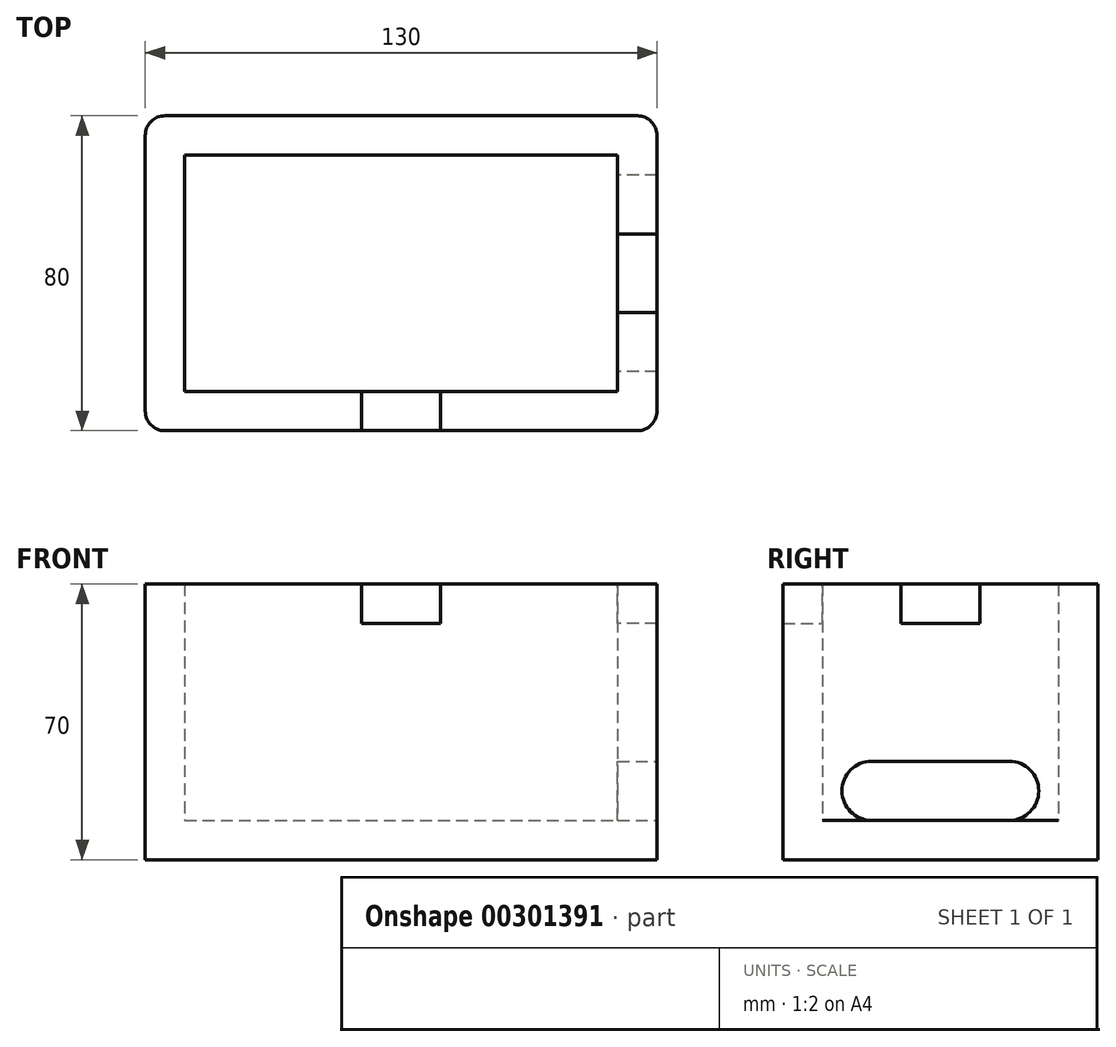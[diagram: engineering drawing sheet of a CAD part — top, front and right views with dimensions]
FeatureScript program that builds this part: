
annotation { "Feature Type Name" : "Feature", "Feature Type Description" : "" }
export const myFeature = defineFeature(function(context is Context, id is Id, definition is map)
    precondition{}
    {
        {
            var Q0;
            Q0=qCreatedBy(makeId("Top.planeOp"),FACE);
            var sketch = newSketch(context, id + "F0", { "sketchPlane" : qUnion([Q0])});
            skLineSegment(sketch, "E0", {"start": v(-0.63, 30) * mm, "end": v(-55, 30) * mm});
            skLineSegment(sketch, "E1.MirrorCS", {"start": v(0.63, 30) * mm, "end": v(55, 30) * mm});
            skLineSegment(sketch, "E2.MirrorCS", {"start": v(-0.63, -30) * mm, "end": v(-55, -30) * mm});
            skLineSegment(sketch, "E3.MirrorCS", {"start": v(0.63, -30) * mm, "end": v(55, -30) * mm});
            skLineSegment(sketch, "E4", {"start": v(-55, 30) * mm, "end": v(-55, -30) * mm});
            skLineSegment(sketch, "E5", {"start": v(55, -30) * mm, "end": v(55, 30) * mm});
            skLineSegment(sketch, "E6", {"start": v(-55, 40) * mm, "end": v(55, 40) * mm});
            skLineSegment(sketch, "E7", {"start": v(55, 40) * mm, "end": v(65, 40) * mm});
            skLineSegment(sketch, "E8", {"start": v(65, 40) * mm, "end": v(65, -30) * mm});
            skLineSegment(sketch, "E9", {"start": v(65, -30) * mm, "end": v(65, -40) * mm});
            skLineSegment(sketch, "E10", {"start": v(65, -40) * mm, "end": v(-55, -40) * mm});
            skLineSegment(sketch, "E11", {"start": v(-55, -40) * mm, "end": v(-65, -40) * mm});
            skLineSegment(sketch, "E12", {"start": v(-55, 40) * mm, "end": v(-65, 40) * mm});
            skLineSegment(sketch, "E13", {"start": v(-65, 40) * mm, "end": v(-65, -40) * mm});
            skSolve(sketch);
        }
        {
            var Q0;
            Q0 = qSketchRegion(id + "F0", true);
            extrude(context, id + "F1", {"entities" : qUnion([Q0]), "depth" : 10 * mm});
        }
        {
            var Q0;
            Q0=makeQuery(id+"F1.opExtrude","CAP_FACE",FACE,{"disambiguationData":[OSD([sQuery(id+"F0.wireOp",EDGE,"E6"),sQuery(id+"F0.wireOp",EDGE,"E7"),sQuery(id+"F0.wireOp",EDGE,"E8"),sQuery(id+"F0.wireOp",EDGE,"E9"),sQuery(id+"F0.wireOp",EDGE,"E10"),sQuery(id+"F0.wireOp",EDGE,"E11"),sQuery(id+"F0.wireOp",EDGE,"E12"),sQuery(id+"F0.wireOp",EDGE,"E13")])],"isStart":false});
            var sketch = newSketch(context, id + "F2", { "sketchPlane" : qUnion([Q0])});
            skLineSegment(sketch, "E14", {"start": v(-55, 30) * mm, "end": v(-55, -30) * mm});
            skLineSegment(sketch, "E15", {"start": v(-55, 30) * mm, "end": v(55, 30) * mm});
            skLineSegment(sketch, "E16.MirrorCS", {"start": v(55, 30) * mm, "end": v(55, -30) * mm});
            skLineSegment(sketch, "E17.MirrorCS", {"start": v(-55, -30) * mm, "end": v(55, -30) * mm});
            skLineSegment(sketch, "E18.0.0", {"start": v(65, 40) * mm, "end": v(-65, 40) * mm});
            skLineSegment(sketch, "E18.0.1", {"start": v(-65, 40) * mm, "end": v(-65, -40) * mm});
            skLineSegment(sketch, "E18.0.2", {"start": v(-65, -40) * mm, "end": v(65, -40) * mm});
            skLineSegment(sketch, "E18.0.3", {"start": v(65, -40) * mm, "end": v(65, 40) * mm});
            skPoint(sketch, "E19.orphan", {"position": v(-55, 40) * mm});
            skPoint(sketch, "E20.orphan", {"position": v(-65, 30) * mm});
            skPoint(sketch, "E21.orphan", {"position": v(65, 30) * mm});
            skPoint(sketch, "E22.orphan", {"position": v(55, 40) * mm});
            skPoint(sketch, "E23.orphan", {"position": v(65, -30) * mm});
            skPoint(sketch, "E24.orphan", {"position": v(55, -40) * mm});
            skPoint(sketch, "E25.orphan", {"position": v(-55, -40) * mm});
            skPoint(sketch, "E26.orphan", {"position": v(-65, -30) * mm});
            skSolve(sketch);
        }
        {
            var Q0;
            Q0=makeQuery(id+"F2.imprint","IMPRINT",FACE,{"disambiguationData":[TD([[makeQuery(id+"F2.imprint","IMPRINT",EDGE,{"derivedFrom":sQuery(id+"F2.wireOp",EDGE,"E14")}),-1.0]])]});
            extrude(context, id + "F3", {"entities" : qUnion([Q0]), "operationType" : NewBodyOperationType.ADD, "depth" : 60 * mm});
        }
        {
            var Q0;
            Q0=makeQuery(id+"F3.opExtrude","CAP_FACE",FACE,{"disambiguationData":[OSD([sQuery(id+"F2.wireOp",EDGE,"E14"),sQuery(id+"F2.wireOp",EDGE,"E15"),sQuery(id+"F2.wireOp",EDGE,"E16.MirrorCS"),sQuery(id+"F2.wireOp",EDGE,"E17.MirrorCS"),sQuery(id+"F2.wireOp",EDGE,"E18.0.0"),sQuery(id+"F2.wireOp",EDGE,"E18.0.1"),sQuery(id+"F2.wireOp",EDGE,"E18.0.2"),sQuery(id+"F2.wireOp",EDGE,"E18.0.3")])],"isStart":false});
            var sketch = newSketch(context, id + "F4", { "sketchPlane" : qUnion([Q0])});
            skLineSegment(sketch, "E27.0.0", {"start": v(65, -40) * mm, "end": v(65, 40) * mm});
            skLineSegment(sketch, "E27.0.1", {"start": v(65, 40) * mm, "end": v(-65, 40) * mm});
            skLineSegment(sketch, "E27.0.2", {"start": v(-65, 40) * mm, "end": v(-65, -40) * mm});
            skLineSegment(sketch, "E27.0.3", {"start": v(-65, -40) * mm, "end": v(65, -40) * mm});
            skLineSegment(sketch, "E28", {"start": v(0, 40) * mm, "end": v(-10, 40) * mm});
            skLineSegment(sketch, "E29", {"start": v(-10, 40) * mm, "end": v(-10, 30) * mm});
            skLineSegment(sketch, "E30", {"start": v(-10, 30) * mm, "end": v(10, 30) * mm});
            skLineSegment(sketch, "E31", {"start": v(10, 30) * mm, "end": v(10, 40) * mm});
            skLineSegment(sketch, "E32", {"start": v(10, 40) * mm, "end": v(0, 40) * mm});
            skLineSegment(sketch, "E33.MirrorCS", {"start": v(-10, -40) * mm, "end": v(-10, -30) * mm});
            skLineSegment(sketch, "E34.MirrorCS", {"start": v(10, -30) * mm, "end": v(10, -40) * mm});
            skLineSegment(sketch, "E35", {"start": v(-65, 0) * mm, "end": v(-65, 10) * mm});
            skLineSegment(sketch, "E36", {"start": v(-65, 10) * mm, "end": v(-55, 10) * mm});
            skLineSegment(sketch, "E37.MirrorCS", {"start": v(-65, -10) * mm, "end": v(-55, -10) * mm});
            skLineSegment(sketch, "E38.MirrorCS", {"start": v(65, 10) * mm, "end": v(55, 10) * mm});
            skLineSegment(sketch, "E39.MirrorCS", {"start": v(65, -10) * mm, "end": v(55, -10) * mm});
            skSolve(sketch);
        }
        {
            var Q0;
            Q0=makeQuery(id+"F4.imprint","IMPRINT",FACE,{"disambiguationData":[TD([[makeQuery(id+"F4.imprint","IMPRINT",EDGE,{"derivedFrom":sQuery(id+"F4.wireOp",EDGE,"E28")}),1.0]])]});
            var Q1;
            {var subQ2=sQuery(id+"F4.wireOp",EDGE,"E35");Q1=makeQuery(id+"F4.imprint","IMPRINT",FACE,{"disambiguationData":[TD([[makeQuery(id+"F4.imprint","IMPRINT",EDGE,{"derivedFrom":subQ2}),1.0]])]});}
            var Q2;
            {var subQ0=sQuery(id+"F4.wireOp",EDGE,"E33.MirrorCS");Q2=makeQuery(id+"F4.imprint","IMPRINT",FACE,{"disambiguationData":[TD([[makeQuery(id+"F4.imprint","IMPRINT",EDGE,{"derivedFrom":subQ0}),-1.0]])]});}
            var Q3;
            {var subQ0=sQuery(id+"F4.wireOp",EDGE,"E38.MirrorCS");Q3=makeQuery(id+"F4.imprint","IMPRINT",FACE,{"disambiguationData":[TD([[makeQuery(id+"F4.imprint","IMPRINT",EDGE,{"derivedFrom":subQ0}),1.0]])]});}
            extrude(context, id + "F5", {"entities" : qUnion([Q0, Q1, Q2, Q3]), "operationType" : NewBodyOperationType.REMOVE, "oppositeDirection" : true, "depth" : 10 * mm});
        }
        {
            var Q0;
            Q0=makeQuery(id+"F3.boolean.opBoolean","MERGE",EDGE,{"derivedFrom":[makeQuery(id+"F1.opExtrude","SWEPT_EDGE",EDGE,{"disambiguationData":[OSD([sQuery(id+"F0.wireOp",EDGE,"E11"),sQuery(id+"F0.wireOp",EDGE,"E13")])]}),makeQuery(id+"F3.opExtrude","SWEPT_EDGE",EDGE,{"disambiguationData":[OSD([sQuery(id+"F2.wireOp",EDGE,"E18.0.1"),sQuery(id+"F2.wireOp",EDGE,"E18.0.2")])]})]});
            var Q1;
            Q1=makeQuery(id+"F3.boolean.opBoolean","MERGE",EDGE,{"derivedFrom":[makeQuery(id+"F1.opExtrude","SWEPT_EDGE",EDGE,{"disambiguationData":[OSD([sQuery(id+"F0.wireOp",EDGE,"E9"),sQuery(id+"F0.wireOp",EDGE,"E10")])]}),makeQuery(id+"F3.opExtrude","SWEPT_EDGE",EDGE,{"disambiguationData":[OSD([sQuery(id+"F2.wireOp",EDGE,"E18.0.2"),sQuery(id+"F2.wireOp",EDGE,"E18.0.3")])]})]});
            var Q2;
            Q2=makeQuery(id+"F3.boolean.opBoolean","MERGE",EDGE,{"derivedFrom":[makeQuery(id+"F1.opExtrude","SWEPT_EDGE",EDGE,{"disambiguationData":[OSD([sQuery(id+"F0.wireOp",EDGE,"E12"),sQuery(id+"F0.wireOp",EDGE,"E13")])]}),makeQuery(id+"F3.opExtrude","SWEPT_EDGE",EDGE,{"disambiguationData":[OSD([sQuery(id+"F2.wireOp",EDGE,"E18.0.0"),sQuery(id+"F2.wireOp",EDGE,"E18.0.1")])]})]});
            var Q3;
            Q3=makeQuery(id+"F3.boolean.opBoolean","MERGE",EDGE,{"derivedFrom":[makeQuery(id+"F1.opExtrude","SWEPT_EDGE",EDGE,{"disambiguationData":[OSD([sQuery(id+"F0.wireOp",EDGE,"E7"),sQuery(id+"F0.wireOp",EDGE,"E8")])]}),makeQuery(id+"F3.opExtrude","SWEPT_EDGE",EDGE,{"disambiguationData":[OSD([sQuery(id+"F2.wireOp",EDGE,"E18.0.0"),sQuery(id+"F2.wireOp",EDGE,"E18.0.3")])]})]});
            fillet(context, id + "F6", {"entities" : qUnion([Q0, Q1, Q2, Q3]), "radius" : 5 * mm, "tangentPropagation" : true, "allowEdgeOverflow" : false});
        }
        {
            var Q0;
            Q0=makeQuery(id+"F3.boolean.opBoolean","MERGE",FACE,{"derivedFrom":[makeQuery(id+"F1.opExtrude","SWEPT_FACE",FACE,{"disambiguationData":[OSD([sQuery(id+"F0.wireOp",EDGE,"E8"),sQuery(id+"F0.wireOp",EDGE,"E9")])]}),makeQuery(id+"F3.opExtrude","SWEPT_FACE",FACE,{"disambiguationData":[OSD([sQuery(id+"F2.wireOp",EDGE,"E18.0.3")])]})]});
            var sketch = newSketch(context, id + "F7", { "sketchPlane" : qUnion([Q0])});
            skLineSegment(sketch, "E40", {"start": v(0, 0) * mm, "end": v(0, 10) * mm});
            skLineSegment(sketch, "E41", {"start": v(0, 10) * mm, "end": v(-25, 10) * mm});
            skLineSegment(sketch, "E42", {"start": v(-25, 10) * mm, "end": v(-25, 25) * mm});
            skLineSegment(sketch, "E43", {"start": v(-25, 25) * mm, "end": v(25, 25) * mm});
            skLineSegment(sketch, "E44", {"start": v(25, 25) * mm, "end": v(25, 10) * mm});
            skLineSegment(sketch, "E45", {"start": v(25, 10) * mm, "end": v(0, 10) * mm});
            skSolve(sketch);
        }
        {
            var Q0;
            Q0 = qSketchRegion(id + "F7", true);
            extrude(context, id + "F8", {"entities" : qUnion([Q0]), "operationType" : NewBodyOperationType.REMOVE, "oppositeDirection" : true, "depth" : 25 * mm});
        }
        {
            var Q0;
            Q0=makeQuery(id+"F8.boolean.opBoolean","COPY",EDGE,{"derivedFrom":makeQuery(id+"F8.opExtrude","SWEPT_EDGE",EDGE,{"disambiguationData":[OSD([sQuery(id+"F7.wireOp",EDGE,"E43"),sQuery(id+"F7.wireOp",EDGE,"E44")])]})});
            var Q1;
            Q1=makeQuery(id+"F8.boolean.opBoolean","COPY",EDGE,{"derivedFrom":makeQuery(id+"F8.opExtrude","SWEPT_EDGE",EDGE,{"disambiguationData":[OSD([sQuery(id+"F7.wireOp",EDGE,"E44"),sQuery(id+"F7.wireOp",EDGE,"E45")])]})});
            var Q2;
            Q2=makeQuery(id+"F8.boolean.opBoolean","COPY",EDGE,{"derivedFrom":makeQuery(id+"F8.opExtrude","SWEPT_EDGE",EDGE,{"disambiguationData":[OSD([sQuery(id+"F7.wireOp",EDGE,"E41"),sQuery(id+"F7.wireOp",EDGE,"E42")])]})});
            var Q3;
            Q3=makeQuery(id+"F8.boolean.opBoolean","COPY",EDGE,{"derivedFrom":makeQuery(id+"F8.opExtrude","SWEPT_EDGE",EDGE,{"disambiguationData":[OSD([sQuery(id+"F7.wireOp",EDGE,"E42"),sQuery(id+"F7.wireOp",EDGE,"E43")])]})});
            fillet(context, id + "F9", {"entities" : qUnion([Q0, Q1, Q2, Q3]), "radius" : 7.5 * mm, "tangentPropagation" : true, "allowEdgeOverflow" : false});
        }
    });
